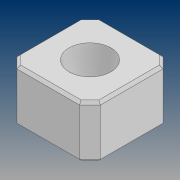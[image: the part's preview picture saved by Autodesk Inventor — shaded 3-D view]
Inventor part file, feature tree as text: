
AUTODESK INVENTOR PART (.ipt)
format: ipt  version: 2021 (Build 250183000, 183)  size: 107,520 bytes
history: native  units: mm
features: chamfer x2, extrude x1, sketch x1
ambient origin geometry x8: Origin, YZ Plane, XZ Plane, XY Plane, X Axis, Y Axis, Z Axis, Center Point
bodies: Solid1 (feature_tree)
feature tree (4):
  extrude  "Extrusion1"  Depth=10.0mm
  chamfer  "Chamfer1"  Distance=10.0mm
  chamfer  "Chamfer2"  Distance=2.0mm Angle=45.0deg
  sketch  "Sketch1"  dims[d0=16.0mm d1=8.0mm d2=10.0mm d3=0.0mm d4=2.0mm d5=2.0mm d6=45.0deg d7=0.5mm d8=2.0mm d9=45.0deg]
